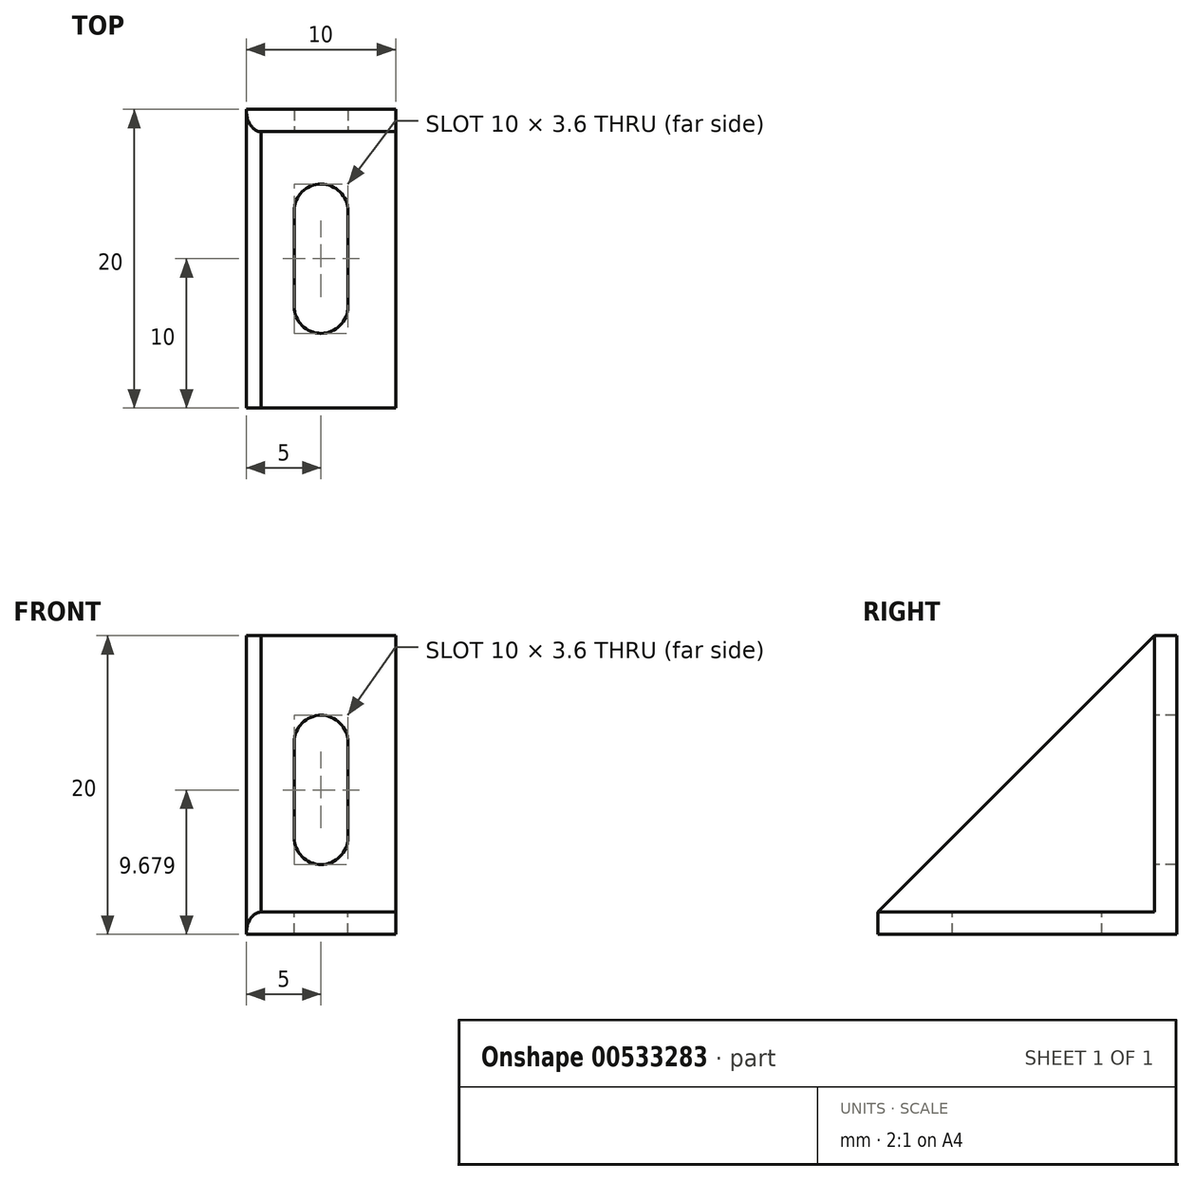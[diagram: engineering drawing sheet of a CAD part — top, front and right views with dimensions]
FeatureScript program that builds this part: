
annotation { "Feature Type Name" : "Feature", "Feature Type Description" : "" }
export const myFeature = defineFeature(function(context is Context, id is Id, definition is map)
    precondition{}
    {
        {
            var Q0;
            Q0=qCreatedBy(makeId("Top.planeOp"),FACE);
            var sketch = newSketch(context, id + "F0", { "sketchPlane" : qUnion([Q0])});
            skLineSegment(sketch, "E0.bottom", {"start": v(5, -10) * mm, "end": v(-5, -10) * mm});
            skLineSegment(sketch, "E0.top", {"start": v(5, 10) * mm, "end": v(-5, 10) * mm});
            skLineSegment(sketch, "E0.left", {"start": v(5, -10) * mm, "end": v(5, 10) * mm});
            skLineSegment(sketch, "E0.right", {"start": v(-5, -10) * mm, "end": v(-5, 10) * mm});
            skPoint(sketch, "E0.middle", {"position": v(0, 0) * mm});
            skSolve(sketch);
        }
        {
            var Q0;
            Q0=makeQuery(id+"F0.imprint","IMPRINT",FACE,{"disambiguationData":[TD([[makeQuery(id+"F0.imprint","IMPRINT",EDGE,{"derivedFrom":sQuery(id+"F0.wireOp",EDGE,"E0.bottom")}),-1.0]])]});
            extrude(context, id + "F1", {"entities" : qUnion([Q0]), "depth" : 1.5 * mm, "offsetDistance" : 25 * mm});
        }
        {
            var Q0;
            Q0=makeQuery(id+"F1.opExtrude","CAP_FACE",FACE,{"disambiguationData":[OSD([sQuery(id+"F0.wireOp",EDGE,"E0.bottom"),sQuery(id+"F0.wireOp",EDGE,"E0.top"),sQuery(id+"F0.wireOp",EDGE,"E0.left"),sQuery(id+"F0.wireOp",EDGE,"E0.right")])],"isStart":false});
            var sketch = newSketch(context, id + "F2", { "sketchPlane" : qUnion([Q0])});
            skLineSegment(sketch, "E1.bottom", {"start": v(-5, 10) * mm, "end": v(5, 10) * mm});
            skLineSegment(sketch, "E1.top", {"start": v(-5, 8.5) * mm, "end": v(5, 8.5) * mm});
            skLineSegment(sketch, "E1.left", {"start": v(-5, 10) * mm, "end": v(-5, 8.5) * mm});
            skLineSegment(sketch, "E1.right", {"start": v(5, 10) * mm, "end": v(5, 8.5) * mm});
            skSolve(sketch);
        }
        {
            var Q0;
            Q0=makeQuery(id+"F2.imprint","IMPRINT",FACE,{"disambiguationData":[TD([[makeQuery(id+"F2.imprint","IMPRINT",EDGE,{"derivedFrom":sQuery(id+"F2.wireOp",EDGE,"E1.bottom")}),1.0]])]});
            extrude(context, id + "F3", {"entities" : qUnion([Q0]), "operationType" : NewBodyOperationType.ADD, "depth" : 18.5 * mm, "offsetDistance" : 25 * mm});
        }
        {
            var Q0;
            Q0=makeQuery(id+"F1.opExtrude","CAP_FACE",FACE,{"disambiguationData":[OSD([sQuery(id+"F0.wireOp",EDGE,"E0.bottom"),sQuery(id+"F0.wireOp",EDGE,"E0.top"),sQuery(id+"F0.wireOp",EDGE,"E0.left"),sQuery(id+"F0.wireOp",EDGE,"E0.right")])],"isStart":false});
            var sketch = newSketch(context, id + "F4", { "sketchPlane" : qUnion([Q0])});
            skLineSegment(sketch, "E2.bottom", {"start": v(0, -5) * mm, "end": v(0, -5) * mm});
            skLineSegment(sketch, "E2.top", {"start": v(0, 5) * mm, "end": v(0, 5) * mm});
            skLineSegment(sketch, "E2.left", {"start": v(1.8, -3.2) * mm, "end": v(1.8, 3.2) * mm});
            skLineSegment(sketch, "E2.right", {"start": v(-1.8, -3.2) * mm, "end": v(-1.8, 3.2) * mm});
            skPoint(sketch, "E2.middle", {"position": v(0, 0) * mm});
            skPoint(sketch, "E3.visualSharp", {"position": v(-1.8, 5) * mm});
            skArc(sketch, "E3.filletArc", {"start": v(0, 5) * mm, "mid": v(-1.27, 4.47) * mm, "end": v(-1.8, 3.2) * mm});
            skPoint(sketch, "E4.visualSharp", {"position": v(1.8, 5) * mm});
            skArc(sketch, "E4.filletArc", {"start": v(1.8, 3.2) * mm, "mid": v(1.27, 4.47) * mm, "end": v(0, 5) * mm});
            skPoint(sketch, "E5.visualSharp", {"position": v(-1.8, -5) * mm});
            skArc(sketch, "E5.filletArc", {"start": v(-1.8, -3.2) * mm, "mid": v(-1.27, -4.47) * mm, "end": v(0, -5) * mm});
            skPoint(sketch, "E6.visualSharp", {"position": v(1.8, -5) * mm});
            skArc(sketch, "E6.filletArc", {"start": v(0, -5) * mm, "mid": v(1.27, -4.47) * mm, "end": v(1.8, -3.2) * mm});
            skSolve(sketch);
        }
        {
            var Q0;
            Q0=makeQuery(id+"F4.imprint","IMPRINT",FACE,{"disambiguationData":[TD([[makeQuery(id+"F4.imprint","IMPRINT",EDGE,{"derivedFrom":sQuery(id+"F4.wireOp",EDGE,"E2.left")}),1.0]])]});
            extrude(context, id + "F5", {"entities" : qUnion([Q0]), "operationType" : NewBodyOperationType.REMOVE, "endBound" : BoundingType.THROUGH_ALL, "oppositeDirection" : true, "depth" : 25 * mm, "offsetDistance" : 25 * mm});
        }
        {
            var Q0;
            Q0=makeQuery(id+"F3.opExtrude","SWEPT_FACE",FACE,{"disambiguationData":[OSD([sQuery(id+"F2.wireOp",EDGE,"E1.top")])]});
            var sketch = newSketch(context, id + "F6", { "sketchPlane" : qUnion([Q0])});
            skLineSegment(sketch, "E7.bottom", {"start": v(0, 4.68) * mm, "end": v(0, 4.68) * mm});
            skLineSegment(sketch, "E7.top", {"start": v(0, 14.68) * mm, "end": v(0, 14.68) * mm});
            skLineSegment(sketch, "E7.left", {"start": v(1.8, 6.48) * mm, "end": v(1.8, 12.88) * mm});
            skLineSegment(sketch, "E7.right", {"start": v(-1.8, 6.48) * mm, "end": v(-1.8, 12.88) * mm});
            skPoint(sketch, "E7.middle", {"position": v(0, 9.68) * mm});
            skPoint(sketch, "E8.visualSharp", {"position": v(-1.8, 14.68) * mm});
            skArc(sketch, "E8.filletArc", {"start": v(0, 14.68) * mm, "mid": v(-1.27, 14.15) * mm, "end": v(-1.8, 12.88) * mm});
            skPoint(sketch, "E9.visualSharp", {"position": v(1.8, 14.68) * mm});
            skArc(sketch, "E9.filletArc", {"start": v(1.8, 12.88) * mm, "mid": v(1.27, 14.15) * mm, "end": v(0, 14.68) * mm});
            skPoint(sketch, "E10.visualSharp", {"position": v(-1.8, 4.68) * mm});
            skArc(sketch, "E10.filletArc", {"start": v(-1.8, 6.48) * mm, "mid": v(-1.27, 5.2) * mm, "end": v(0, 4.68) * mm});
            skPoint(sketch, "E11.visualSharp", {"position": v(1.8, 4.68) * mm});
            skArc(sketch, "E11.filletArc", {"start": v(0, 4.68) * mm, "mid": v(1.27, 5.2) * mm, "end": v(1.8, 6.48) * mm});
            skSolve(sketch);
        }
        {
            var Q0;
            Q0=makeQuery(id+"F6.imprint","IMPRINT",FACE,{"disambiguationData":[TD([[makeQuery(id+"F6.imprint","IMPRINT",EDGE,{"derivedFrom":sQuery(id+"F6.wireOp",EDGE,"E7.left")}),1.0]])]});
            extrude(context, id + "F7", {"entities" : qUnion([Q0]), "operationType" : NewBodyOperationType.REMOVE, "endBound" : BoundingType.THROUGH_ALL, "oppositeDirection" : true, "depth" : 25 * mm, "offsetDistance" : 25 * mm});
        }
        {
            var Q0;
            Q0=makeQuery(id+"F3.boolean.opBoolean","MERGE",FACE,{"derivedFrom":[makeQuery(id+"F1.opExtrude","SWEPT_FACE",FACE,{"disambiguationData":[OSD([sQuery(id+"F0.wireOp",EDGE,"E0.right")])]}),makeQuery(id+"F3.opExtrude","SWEPT_FACE",FACE,{"disambiguationData":[OSD([sQuery(id+"F2.wireOp",EDGE,"E1.left")])]})]});
            var sketch = newSketch(context, id + "F8", { "sketchPlane" : qUnion([Q0])});
            skLineSegment(sketch, "E12", {"start": v(-8.5, 20) * mm, "end": v(-8.5, 1.5) * mm});
            skLineSegment(sketch, "E13", {"start": v(-8.5, 1.5) * mm, "end": v(10, 1.5) * mm});
            skLineSegment(sketch, "E14", {"start": v(10, 1.5) * mm, "end": v(-8.5, 20) * mm});
            skSolve(sketch);
        }
        {
            var Q0;
            Q0=makeQuery(id+"F8.imprint","IMPRINT",FACE,{"disambiguationData":[TD([[makeQuery(id+"F8.imprint","IMPRINT",EDGE,{"derivedFrom":sQuery(id+"F8.wireOp",EDGE,"E12")}),1.0]])]});
            extrude(context, id + "F9", {"entities" : qUnion([Q0]), "operationType" : NewBodyOperationType.ADD, "oppositeDirection" : true, "depth" : 1 * mm, "offsetDistance" : 25 * mm});
        }
        {
            var Q0;
            Q0=makeQuery(id+"F9.opExtrude","CAP_EDGE",EDGE,{"disambiguationData":[OSD([sQuery(id+"F8.wireOp",EDGE,"E14")])],"isStart":true});
            var Q1;
            Q1=makeQuery(id+"FfZY0uCbZ2WBckC_1.1.F9.opExtrude","CAP_EDGE",EDGE,{"disambiguationData":[OSD([sQuery(id+"F8.wireOp",EDGE,"E14")])],"isStart":true});
            fillet(context, id + "F10", {"entities" : qUnion([Q0, Q1]), "radius" : 1 * mm, "tangentPropagation" : true, "allowEdgeOverflow" : false});
        }
    });
